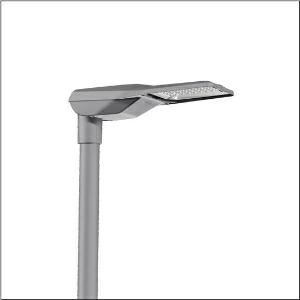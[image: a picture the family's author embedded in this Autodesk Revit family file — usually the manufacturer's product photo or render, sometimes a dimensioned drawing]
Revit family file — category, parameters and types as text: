
# Revit family: streetlight_sl_21_mini___pl52_5xe6h33a08gb_e896
name_source: partatom
category: Lighting Fixtures
units: mm (PartAtom-declared; Revit-internal decimal feet)

## family parameters
Cut with Voids When Loaded = No
Host = Face
Light Source = No
Part Type = Normal
Room Calculation Point = No
Round Connector Dimension = Use Diameter
Shared = No

## types (1)
- --- (1 x LED, 5840 lm, 40.4 W, 3000K)
    Apparent Load = 40 VA
    CIE Flux Codes = 27 59 98 100 100
    Color Rendering = 70
    Color Temperature = 3000K
    Default Elevation = 1800 mm
    Description = Streetlight SL 21 mini, mast luminaire, primary light control with lens, of PMMA, primary optical cover: cover, of toughened safety glass, transparent, light distribution: PL52, light emission: direct distribution, primary light characteristic: asymmetric, installation type: post-top, side-entry, LED, 3G 1.5mm², High Power LED, rated luminous flux: 5.840lm, luminous efficacy: 145lm/W, light colour: 730, colour temperature: 3000K, control: overheat protection, constant luminous flux control, time-dependent luminous flux control, flexible luminous flux parameterisation, mains connection: 230..240V, AC, 50/60Hz, connection cable pre-assembled, cable length: 6,5m, wiring characteristics: H07RN-F, start of lifetime: 40W, end of service life: 41W, reduction: 19W, luminaire housing, of diecast aluminium, powder-coated, Siteco® metallic grey (DB 702S), corrosivity category C5 mid according to DIN EN ISO 12944, please order mast flange separately, inclination adjustable: 0°, 5°, 10°, 15°, sealing non-destructively replaceable, multi-level sealing system, length: 628mm, width: 235mm, height: 110mm, mast flange for spigot size: 42mm (side-entry): 5XC10008XM4, 60/48mm (side-entry/post-top): 5XC10108XM2, 76/60mm (side-entry/post-top): 5XC10108XM1, protection rating (complete): IP66, insulation class (complete): insulation class II (safety insulation), certification: CE, ENEC, ENEC+, VDE, impact resistance: IK09, permissible operating ambient temperature for outdoor applications: -40..+50°C, standard-compliant lighting for roads and squares, packaging unit: 1 piece

Light Distribution: PL52
    Height = 110 mm
    Lamp = 1 x LED
    Lamp Light Flux = 5840 lm
    Lamp Power = 40.4 W
    Lamp count = 1
    Length = 625 mm
    Luminous efficacy = 145 lm/W
    Manufacturer = Siteco
    ModVariant = No
    Model = 5XE6H33A08GB
    Number of Poles = 1
    OnlyDefault = Yes
    Power Factor = 1
    Product Name = Streetlight SL 21 mini | PL52
    Product group = mast luminaire | pylon top
    ProductGroupID = 6100
    Protection Class = Protection class II
    Protection Degree = IP 66
    RLX_Detail_Level = 1
    RLX_Emergency_Light_Flux = 0 lm
    RLX_Emergency_Type = 0
    RLX_Emergency_Type_DB = No
    RlxData = <blob elided: 102077 chars, md5=cb17a656>
    Socket = socket
    Standby Power = 0 W
    System Light Flux = 5840 lm
    System Power = 40 W
    Type Comments = factory setting: luminous flux: 100 % | Output Level: 100 % | 812 mA
    Type Image = l_1003519.jpg
    URL = http://relux.com
    VarID = @adj_123903
    Voltage = 0 V
    Weight = 0.00 kg
    Width = 234 mm

## geometry (parser evidence)
native form markers: Blend x4, Sweep x10
no freeform markers — native parametric forms only
